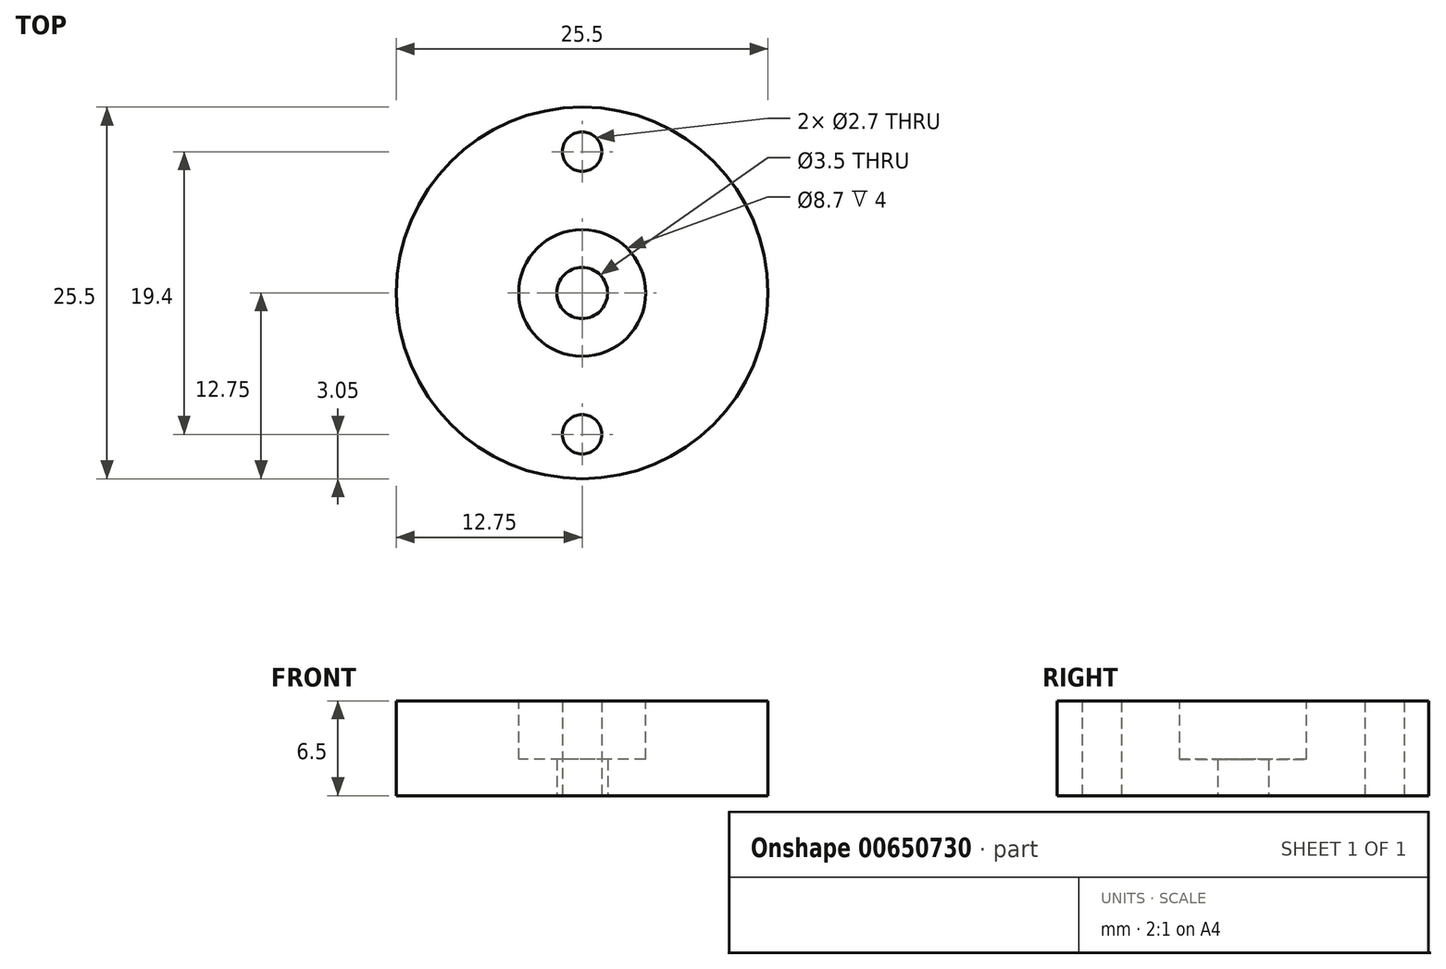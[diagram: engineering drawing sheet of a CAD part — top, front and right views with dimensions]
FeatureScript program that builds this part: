
annotation { "Feature Type Name" : "Feature", "Feature Type Description" : "" }
export const myFeature = defineFeature(function(context is Context, id is Id, definition is map)
    precondition{}
    {
        {
            var Q0;
            Q0=qCreatedBy(makeId("Top.planeOp"),FACE);
            var sketch = newSketch(context, id + "F0", { "sketchPlane" : qUnion([Q0])});
            skCircle(sketch, "E0", {"center": v(0, 0) * mm, "radius": 12.75 * mm});
            skCircle(sketch, "E1", {"center": v(0, 9.7) * mm, "radius": 1.35 * mm});
            skCircle(sketch, "E2", {"center": v(0, -9.7) * mm, "radius": 1.35 * mm});
            skCircle(sketch, "E3", {"center": v(0, 0) * mm, "radius": 1.75 * mm});
            skSolve(sketch);
        }
        {
            var Q0;
            Q0 = qSketchRegion(id + "F0", true);
            extrude(context, id + "F1", {"entities" : qUnion([Q0]), "depth" : 6.5 * mm, "offsetDistance" : 25 * mm});
        }
        {
            var Q0;
            Q0=makeQuery(id+"F1.opExtrude","CAP_FACE",FACE,{"disambiguationData":[OSD([sQuery(id+"F0.wireOp",EDGE,"E0"),sQuery(id+"F0.wireOp",EDGE,"E1"),sQuery(id+"F0.wireOp",EDGE,"E2"),sQuery(id+"F0.wireOp",EDGE,"E3")])],"isStart":false});
            var sketch = newSketch(context, id + "F2", { "sketchPlane" : qUnion([Q0])});
            skCircle(sketch, "E4", {"center": v(0, 0) * mm, "radius": 4.35 * mm});
            skSolve(sketch);
        }
        {
            var Q0;
            Q0 = qSketchRegion(id + "F2", true);
            extrude(context, id + "F3", {"entities" : qUnion([Q0]), "operationType" : NewBodyOperationType.REMOVE, "oppositeDirection" : true, "depth" : 4 * mm, "offsetDistance" : 25 * mm});
        }
    });
